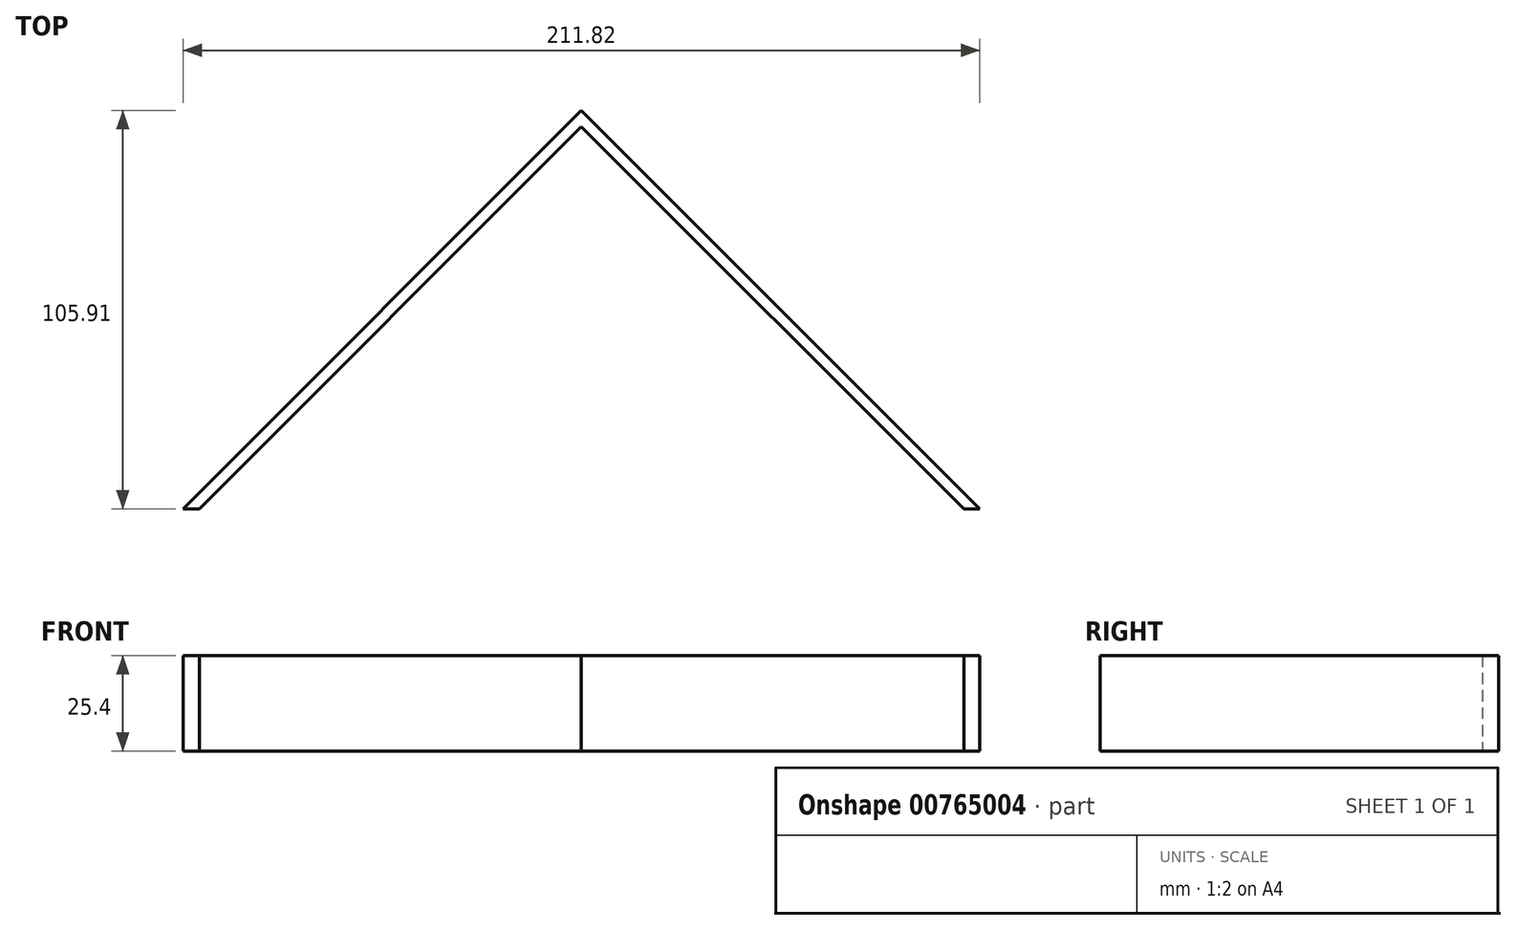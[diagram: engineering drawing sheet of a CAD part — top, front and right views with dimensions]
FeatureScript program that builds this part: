
annotation { "Feature Type Name" : "Feature", "Feature Type Description" : "" }
export const myFeature = defineFeature(function(context is Context, id is Id, definition is map)
    precondition{}
    {
        {
            var Q0;
            Q0=qCreatedBy(makeId("Top.planeOp"),FACE);
            var sketch = newSketch(context, id + "F0", { "sketchPlane" : qUnion([Q0])});
            skLineSegment(sketch, "E0", {"start": v(101.6, 0) * mm, "end": v(0, 101.6) * mm});
            skLineSegment(sketch, "E1", {"start": v(0, 101.6) * mm, "end": v(-101.6, 0) * mm});
            skLineSegment(sketch, "E2", {"start": v(101.6, 0) * mm, "end": v(105.91, 0) * mm});
            skLineSegment(sketch, "E3", {"start": v(105.91, 0) * mm, "end": v(0, 105.91) * mm});
            skLineSegment(sketch, "E4", {"start": v(0, 105.91) * mm, "end": v(-105.91, 0) * mm});
            skLineSegment(sketch, "E5", {"start": v(-105.91, 0) * mm, "end": v(-101.6, 0) * mm});
            skSolve(sketch);
        }
        {
            var Q0;
            Q0 = qSketchRegion(id + "F0", true);
            extrude(context, id + "F1", {"entities" : qUnion([Q0]), "depth" : 25.4 * mm, "offsetDistance" : 25.4 * mm});
        }
    });
